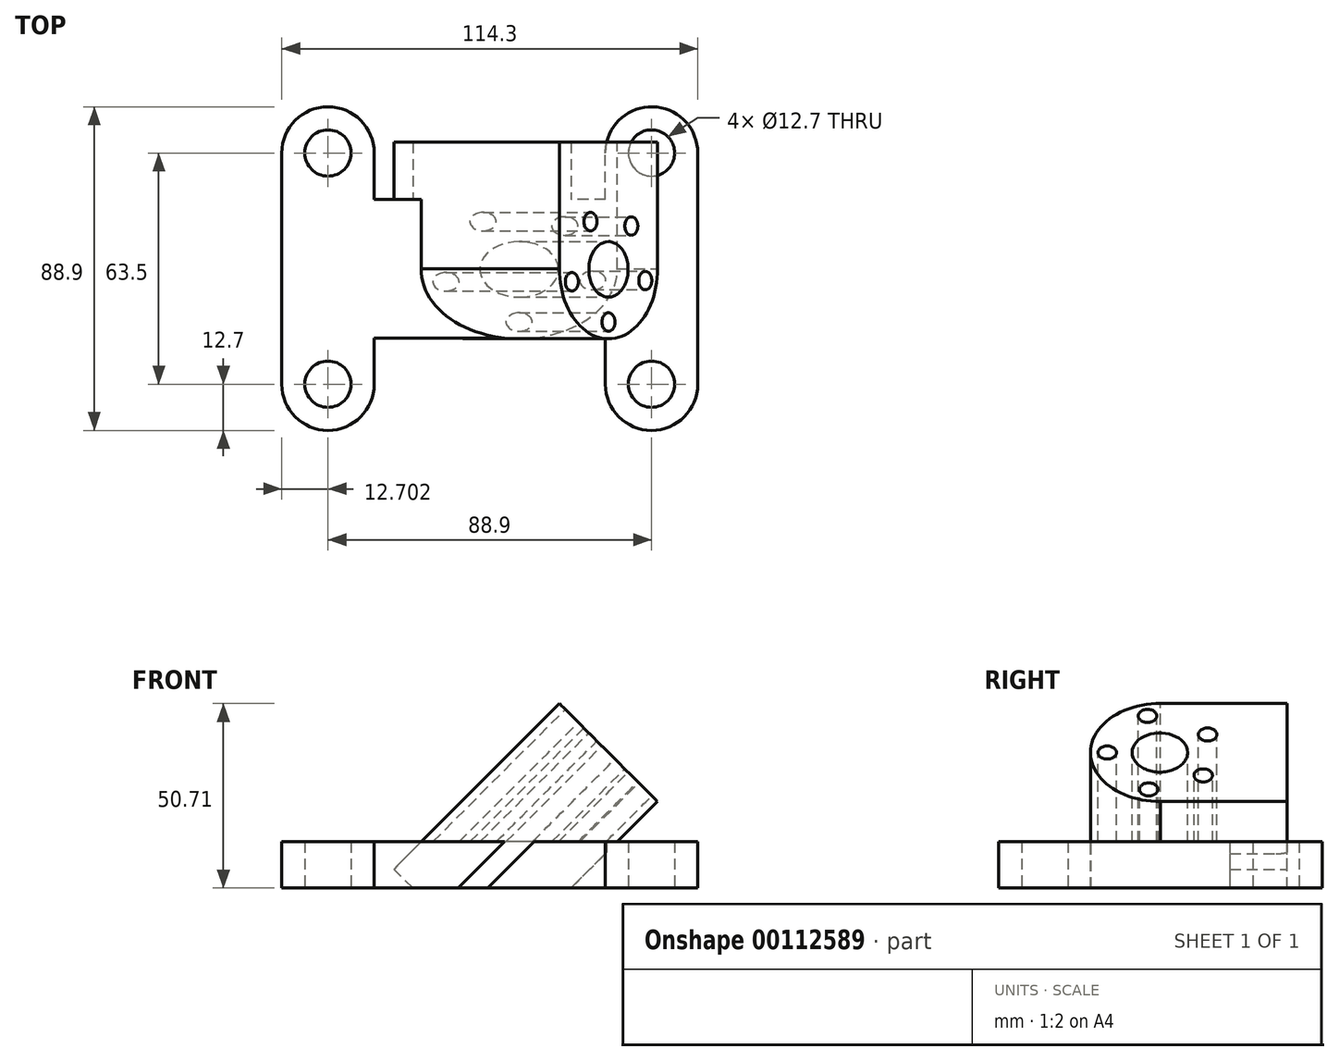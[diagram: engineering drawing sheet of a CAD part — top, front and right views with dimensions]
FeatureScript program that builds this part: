
annotation { "Feature Type Name" : "Feature", "Feature Type Description" : "" }
export const myFeature = defineFeature(function(context is Context, id is Id, definition is map)
    precondition{}
    {
        {
            var Q0;
            Q0=qCreatedBy(makeId("Top.planeOp"),FACE);
            var sketch = newSketch(context, id + "F0", { "sketchPlane" : qUnion([Q0])});
            skLineSegment(sketch, "E0", {"start": v(-46.17, 0) * mm, "end": v(42.73, 0) * mm, "construction": true});
            skLineSegment(sketch, "E1", {"start": v(-46.17, -31.75) * mm, "end": v(-46.17, 31.75) * mm, "construction": true});
            skLineSegment(sketch, "E2", {"start": v(42.73, -31.75) * mm, "end": v(42.73, 31.75) * mm, "construction": true});
            skCircle(sketch, "E3", {"center": v(-46.17, 31.75) * mm, "radius": 6.35 * mm});
            skCircle(sketch, "E4", {"center": v(42.73, 31.75) * mm, "radius": 6.35 * mm});
            skCircle(sketch, "E5", {"center": v(-46.17, -31.75) * mm, "radius": 6.35 * mm});
            skCircle(sketch, "E6", {"center": v(42.73, -31.75) * mm, "radius": 6.35 * mm});
            skArc(sketch, "E7", {"start": v(-33.47, 31.75) * mm, "mid": v(-46.17, 44.45) * mm, "end": v(-58.87, 31.75) * mm});
            skArc(sketch, "E8", {"start": v(55.43, 31.75) * mm, "mid": v(42.73, 44.45) * mm, "end": v(30.03, 31.75) * mm});
            skArc(sketch, "E9", {"start": v(-58.87, -31.75) * mm, "mid": v(-46.17, -44.45) * mm, "end": v(-33.47, -31.75) * mm});
            skArc(sketch, "E10", {"start": v(30.03, -31.75) * mm, "mid": v(42.73, -44.45) * mm, "end": v(55.43, -31.75) * mm});
            skLineSegment(sketch, "E11", {"start": v(55.43, -31.75) * mm, "end": v(55.43, 31.75) * mm});
            skLineSegment(sketch, "E12", {"start": v(-58.87, -31.75) * mm, "end": v(-58.87, 31.75) * mm});
            skLineSegment(sketch, "E13", {"start": v(-33.47, 31.75) * mm, "end": v(-33.47, 19.05) * mm});
            skLineSegment(sketch, "E14", {"start": v(-33.47, -31.75) * mm, "end": v(-33.47, -19.05) * mm});
            skLineSegment(sketch, "E15", {"start": v(30.03, -31.75) * mm, "end": v(30.03, -19.05) * mm});
            skLineSegment(sketch, "E16", {"start": v(30.03, 31.75) * mm, "end": v(30.03, 19.05) * mm});
            skLineSegment(sketch, "E17", {"start": v(-33.47, -19.05) * mm, "end": v(30.03, -19.05) * mm});
            skLineSegment(sketch, "E18", {"start": v(-33.47, 19.05) * mm, "end": v(30.03, 19.05) * mm});
            skSolve(sketch);
        }
        {
            var Q0;
            Q0 = qSketchRegion(id + "F0", true);
            extrude(context, id + "F1", {"entities" : qUnion([Q0]), "endBound" : BoundingType.SYMMETRIC, "depth" : 12.7 * mm});
        }
        {
            var Q0;
            Q0=makeQuery(id+"F1.opExtrude","CAP_EDGE",EDGE,{"disambiguationData":[OSD([sQuery(id+"F0.wireOp",EDGE,"E11")])],"isStart":false});
            cPlane(context, id + "F2", {"entities" : qUnion([Q0]), "cplaneType" : CPlaneType.LINE_ANGLE, "offset" : 25.4 * mm, "angle" : 45 * degree, "width" : 152.4 * mm, "height" : 152.4 * mm});
        }
        {
            var Q0;
            Q0=qCreatedBy(id+"F2.planeOp",FACE);
            var sketch = newSketch(context, id + "F3", { "sketchPlane" : qUnion([Q0])});
            skLineSegment(sketch, "E19.0", {"start": v(34.7, -31.75) * mm, "end": v(34.7, 31.75) * mm});
            skLineSegment(sketch, "E20", {"start": v(34.7, 0) * mm, "end": v(-0.22, 0) * mm, "construction": true});
            skCircle(sketch, "E21", {"center": v(-0.22, 0) * mm, "radius": 7.62 * mm});
            skArc(sketch, "E22", {"start": v(0, 19.05) * mm, "mid": v(-19.27, 0) * mm, "end": v(0, -19.05) * mm});
            skLineSegment(sketch, "E23", {"start": v(0, -19.05) * mm, "end": v(34.7, -19.05) * mm});
            skLineSegment(sketch, "E24", {"start": v(0, 19.05) * mm, "end": v(34.7, 19.05) * mm});
            skCircle(sketch, "E25", {"center": v(-14.68, 0) * mm, "radius": 2.54 * mm});
            skPoint(sketch, "E26.center", {"position": v(0, 0) * mm});
            skLineSegment(sketch, "E26.anchor1", {"start": v(0, 0) * mm, "end": v(-14.68, 0) * mm, "construction": true});
            skLineSegment(sketch, "E26.anchor2", {"start": v(0, 0) * mm, "end": v(7.34, -12.71) * mm, "construction": true});
            skCircle(sketch, "E27.1.0", {"center": v(-3.62, 14.23) * mm, "radius": 2.54 * mm});
            skCircle(sketch, "E27.2.0", {"center": v(12.9, 7) * mm, "radius": 2.54 * mm});
            skLineSegment(sketch, "E27.anchor2", {"start": v(0, 0) * mm, "end": v(12.9, 7) * mm, "construction": true});
            skCircle(sketch, "E28.1.0", {"center": v(11.7, -8.88) * mm, "radius": 2.54 * mm});
            skCircle(sketch, "E28.2.0", {"center": v(-3.29, -14.3) * mm, "radius": 2.54 * mm});
            skLineSegment(sketch, "E28.anchor2", {"start": v(0, 0) * mm, "end": v(-3.29, -14.3) * mm, "construction": true});
            skSolve(sketch);
        }
        {
            var Q0;
            Q0 = qSketchRegion(id + "F3", true);
            extrude(context, id + "F4", {"entities" : qUnion([Q0]), "operationType" : NewBodyOperationType.ADD, "oppositeDirection" : true, "depth" : 64.36 * mm});
        }
        {
            var Q0;
            Q0=qCreatedBy(makeId("Front.planeOp"),FACE);
            var sketch = newSketch(context, id + "F5", { "sketchPlane" : qUnion([Q0])});
            skPoint(sketch, "E29.0", {"position": v(-58.87, -6.35) * mm});
            skPoint(sketch, "E30.0", {"position": v(55.43, -6.35) * mm});
            skLineSegment(sketch, "E31.bottom", {"start": v(-58.87, -6.35) * mm, "end": v(55.53, -6.35) * mm});
            skLineSegment(sketch, "E31.top", {"start": v(-58.87, -43.66) * mm, "end": v(55.53, -43.66) * mm});
            skLineSegment(sketch, "E31.left", {"start": v(-58.87, -6.35) * mm, "end": v(-58.87, -43.66) * mm});
            skLineSegment(sketch, "E31.right", {"start": v(55.53, -6.35) * mm, "end": v(55.53, -43.66) * mm});
            skSolve(sketch);
        }
        {
            var Q0;
            Q0 = qSketchRegion(id + "F5", true);
            extrude(context, id + "F6", {"entities" : qUnion([Q0]), "operationType" : NewBodyOperationType.REMOVE, "endBound" : BoundingType.SYMMETRIC, "depth" : 127 * mm});
        }
    });
